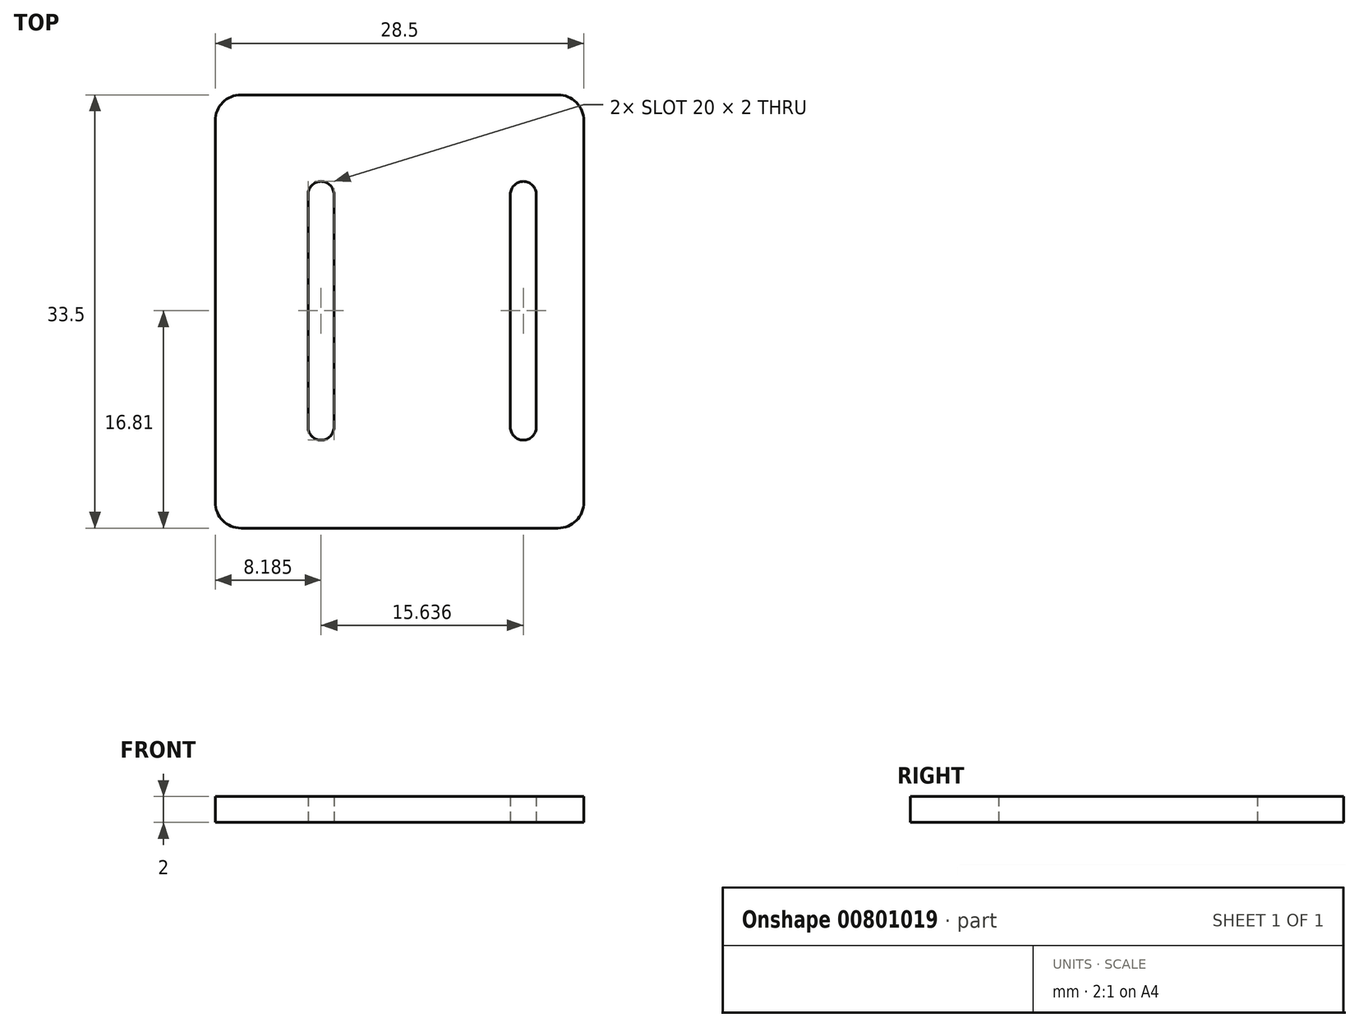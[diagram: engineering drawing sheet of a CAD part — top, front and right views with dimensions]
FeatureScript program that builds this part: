
annotation { "Feature Type Name" : "Feature", "Feature Type Description" : "" }
export const myFeature = defineFeature(function(context is Context, id is Id, definition is map)
    precondition{}
    {
        {
            var Q0;
            Q0=qCreatedBy(makeId("Top.planeOp"),FACE);
            var sketch = newSketch(context, id + "F0", { "sketchPlane" : qUnion([Q0])});
            skLineSegment(sketch, "E0.bottom", {"start": v(-8.82, -6.44) * mm, "end": v(15.68, -6.44) * mm});
            skLineSegment(sketch, "E0.top", {"start": v(-8.82, 27.06) * mm, "end": v(15.68, 27.06) * mm});
            skLineSegment(sketch, "E0.left", {"start": v(-10.82, -4.44) * mm, "end": v(-10.82, 25.06) * mm});
            skLineSegment(sketch, "E0.right", {"start": v(17.68, -4.44) * mm, "end": v(17.68, 25.06) * mm});
            skLineSegment(sketch, "E1.bottom", {"start": v(-2.64, 20.37) * mm, "end": v(-2.64, 20.37) * mm});
            skLineSegment(sketch, "E1.top", {"start": v(-2.64, 0.37) * mm, "end": v(-2.64, 0.37) * mm});
            skLineSegment(sketch, "E1.left", {"start": v(-3.64, 19.37) * mm, "end": v(-3.64, 1.37) * mm});
            skLineSegment(sketch, "E1.right", {"start": v(-1.64, 19.37) * mm, "end": v(-1.64, 1.37) * mm});
            skLineSegment(sketch, "E2.bottom", {"start": v(13, 20.37) * mm, "end": v(13, 20.37) * mm});
            skLineSegment(sketch, "E2.top", {"start": v(13, 0.37) * mm, "end": v(13, 0.37) * mm});
            skLineSegment(sketch, "E2.left", {"start": v(12, 19.37) * mm, "end": v(12, 1.37) * mm});
            skLineSegment(sketch, "E2.right", {"start": v(14, 19.37) * mm, "end": v(14, 1.37) * mm});
            skPoint(sketch, "E3.visualSharp", {"position": v(-10.82, 27.06) * mm});
            skArc(sketch, "E3.filletArc", {"start": v(-8.82, 27.06) * mm, "mid": v(-10.23, 26.48) * mm, "end": v(-10.82, 25.06) * mm});
            skPoint(sketch, "E4.visualSharp", {"position": v(17.68, 27.06) * mm});
            skArc(sketch, "E4.filletArc", {"start": v(17.68, 25.06) * mm, "mid": v(17.1, 26.48) * mm, "end": v(15.68, 27.06) * mm});
            skPoint(sketch, "E5.visualSharp", {"position": v(17.68, -6.44) * mm});
            skArc(sketch, "E5.filletArc", {"start": v(15.68, -6.44) * mm, "mid": v(17.1, -5.85) * mm, "end": v(17.68, -4.44) * mm});
            skPoint(sketch, "E6.visualSharp", {"position": v(-10.82, -6.44) * mm});
            skArc(sketch, "E6.filletArc", {"start": v(-10.82, -4.44) * mm, "mid": v(-10.23, -5.85) * mm, "end": v(-8.82, -6.44) * mm});
            skPoint(sketch, "E7.visualSharp", {"position": v(-3.64, 20.37) * mm});
            skArc(sketch, "E7.filletArc", {"start": v(-2.64, 20.37) * mm, "mid": v(-3.34, 20.08) * mm, "end": v(-3.64, 19.37) * mm});
            skPoint(sketch, "E8.visualSharp", {"position": v(-3.64, 0.37) * mm});
            skArc(sketch, "E8.filletArc", {"start": v(-3.64, 1.37) * mm, "mid": v(-3.34, 0.66) * mm, "end": v(-2.64, 0.37) * mm});
            skPoint(sketch, "E9.visualSharp", {"position": v(-1.64, 0.37) * mm});
            skArc(sketch, "E9.filletArc", {"start": v(-2.64, 0.37) * mm, "mid": v(-1.93, 0.66) * mm, "end": v(-1.64, 1.37) * mm});
            skPoint(sketch, "E10.visualSharp", {"position": v(12, 20.37) * mm});
            skArc(sketch, "E10.filletArc", {"start": v(13, 20.37) * mm, "mid": v(12.3, 20.08) * mm, "end": v(12, 19.37) * mm});
            skPoint(sketch, "E11.visualSharp", {"position": v(14, 20.37) * mm});
            skArc(sketch, "E11.filletArc", {"start": v(14, 19.37) * mm, "mid": v(13.7, 20.08) * mm, "end": v(13, 20.37) * mm});
            skPoint(sketch, "E12.visualSharp", {"position": v(14, 0.37) * mm});
            skArc(sketch, "E12.filletArc", {"start": v(13, 0.37) * mm, "mid": v(13.7, 0.66) * mm, "end": v(14, 1.37) * mm});
            skPoint(sketch, "E13.visualSharp", {"position": v(12, 0.37) * mm});
            skArc(sketch, "E13.filletArc", {"start": v(12, 1.37) * mm, "mid": v(12.3, 0.66) * mm, "end": v(13, 0.37) * mm});
            skPoint(sketch, "E14.visualSharp", {"position": v(-1.64, 20.37) * mm});
            skArc(sketch, "E14.filletArc", {"start": v(-1.64, 19.37) * mm, "mid": v(-1.93, 20.08) * mm, "end": v(-2.64, 20.37) * mm});
            skSolve(sketch);
        }
        {
            var Q0;
            Q0=makeQuery(id+"F0.imprint","IMPRINT",FACE,{"disambiguationData":[TD([[makeQuery(id+"F0.imprint","IMPRINT",EDGE,{"derivedFrom":sQuery(id+"F0.wireOp",EDGE,"E0.bottom")}),1.0]])]});
            extrude(context, id + "F1", {"entities" : qUnion([Q0]), "depth" : 2 * mm, "offsetDistance" : 25.4 * mm});
        }
    });
